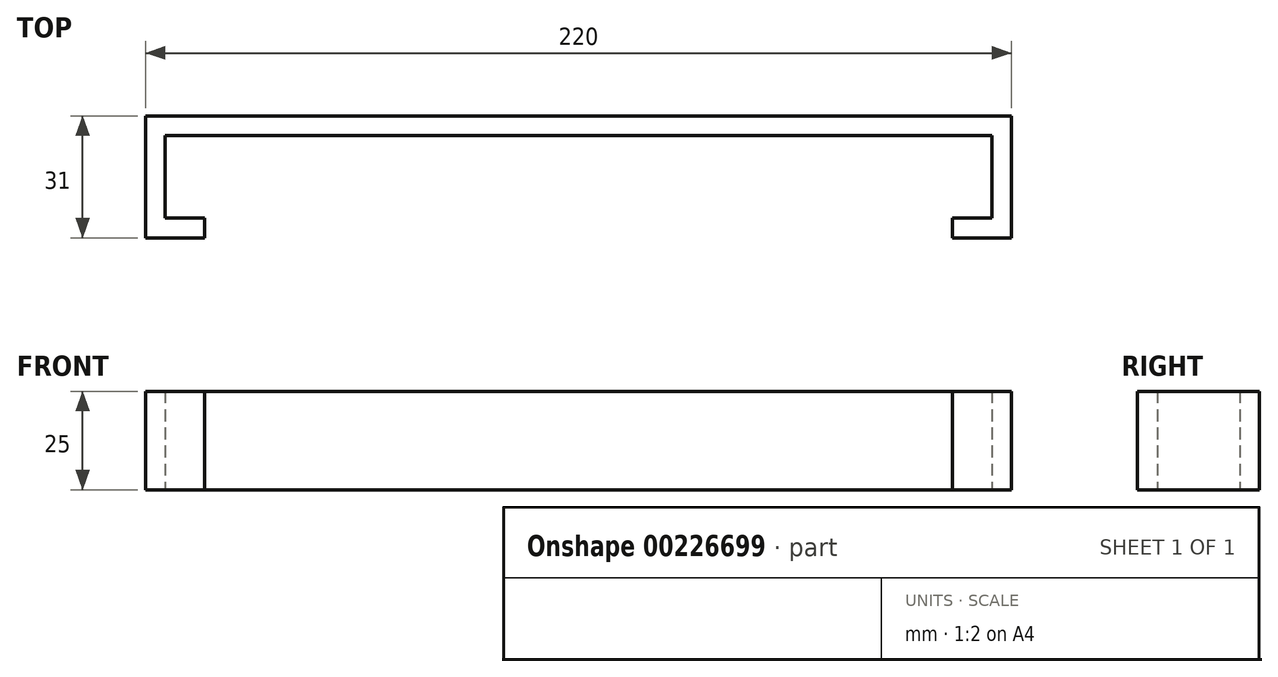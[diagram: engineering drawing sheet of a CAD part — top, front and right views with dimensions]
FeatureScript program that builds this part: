
annotation { "Feature Type Name" : "Feature", "Feature Type Description" : "" }
export const myFeature = defineFeature(function(context is Context, id is Id, definition is map)
    precondition{}
    {
        {
            var Q0;
            Q0=qCreatedBy(makeId("Top.planeOp"),FACE);
            var sketch = newSketch(context, id + "F0", { "sketchPlane" : qUnion([Q0])});
            skLineSegment(sketch, "E0", {"start": v(-105, -38.97) * mm, "end": v(105, -38.97) * mm});
            skLineSegment(sketch, "E1", {"start": v(105, -38.97) * mm, "end": v(105, -59.97) * mm});
            skLineSegment(sketch, "E2", {"start": v(105, -59.97) * mm, "end": v(95, -59.97) * mm});
            skLineSegment(sketch, "E3", {"start": v(95, -59.97) * mm, "end": v(95, -64.97) * mm});
            skLineSegment(sketch, "E4", {"start": v(95, -64.97) * mm, "end": v(110, -64.97) * mm});
            skLineSegment(sketch, "E5", {"start": v(110, -64.97) * mm, "end": v(110, -33.97) * mm});
            skLineSegment(sketch, "E6", {"start": v(110, -33.97) * mm, "end": v(-110, -33.97) * mm});
            skLineSegment(sketch, "E7", {"start": v(-110, -33.97) * mm, "end": v(-110, -64.97) * mm});
            skLineSegment(sketch, "E8", {"start": v(-110, -64.97) * mm, "end": v(-95, -64.97) * mm});
            skLineSegment(sketch, "E9", {"start": v(-95, -64.97) * mm, "end": v(-95, -59.97) * mm});
            skLineSegment(sketch, "E10", {"start": v(-95, -59.97) * mm, "end": v(-105, -59.97) * mm});
            skLineSegment(sketch, "E11", {"start": v(-105, -59.97) * mm, "end": v(-105, -38.97) * mm});
            skSolve(sketch);
        }
        {
            var Q0;
            Q0=makeQuery(id+"F0.imprint","IMPRINT",FACE,{"disambiguationData":[TD([[makeQuery(id+"F0.imprint","IMPRINT",EDGE,{"derivedFrom":sQuery(id+"F0.wireOp",EDGE,"E0")}),1.0]])]});
            extrude(context, id + "F1", {"entities" : qUnion([Q0]), "depth" : 25 * mm, "offsetDistance" : 25 * mm});
        }
    });
